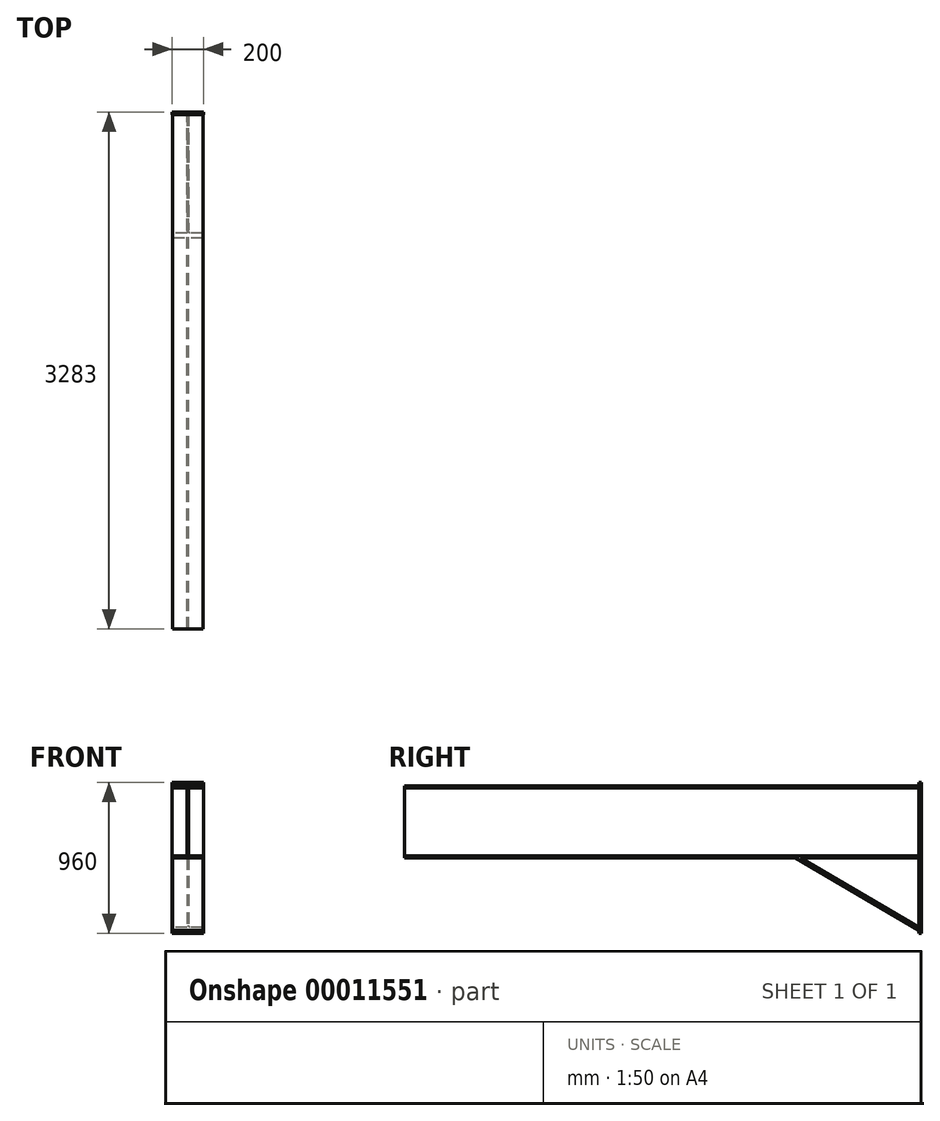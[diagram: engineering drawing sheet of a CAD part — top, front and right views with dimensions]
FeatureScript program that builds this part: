
annotation { "Feature Type Name" : "Feature", "Feature Type Description" : "" }
export const myFeature = defineFeature(function(context is Context, id is Id, definition is map)
    precondition{}
    {
        {
            var Q0;
            Q0=qCreatedBy(makeId("Front.planeOp"),FACE);
            var sketch = newSketch(context, id + "F0", { "sketchPlane" : qUnion([Q0])});
            skLineSegment(sketch, "E0.rect.bottom", {"start": v(95.5, -228.5) * mm, "end": v(-95.5, -228.5) * mm});
            skLineSegment(sketch, "E0.rect.top", {"start": v(95.5, 228.5) * mm, "end": v(-95.5, 228.5) * mm});
            skLineSegment(sketch, "E0.rect.left", {"start": v(95.5, -228.5) * mm, "end": v(95.5, -216.88) * mm});
            skLineSegment(sketch, "E0.rect.right", {"start": v(-95.5, -228.5) * mm, "end": v(-95.5, -216.88) * mm});
            skPoint(sketch, "E0.rect.middle", {"position": v(0, 0) * mm});
            skLineSegment(sketch, "E1", {"start": v(0, 228.5) * mm, "end": v(0, -228.5) * mm});
            skLineSegment(sketch, "E2.0", {"start": v(-4.25, 206.88) * mm, "end": v(-4.25, -206.88) * mm});
            skLineSegment(sketch, "E3.0", {"start": v(4.25, 206.88) * mm, "end": v(4.25, -206.88) * mm});
            skLineSegment(sketch, "E4.0", {"start": v(95.5, 216.88) * mm, "end": v(14.25, 216.88) * mm});
            skLineSegment(sketch, "E5.0", {"start": v(95.5, -216.88) * mm, "end": v(14.25, -216.88) * mm});
            skLineSegment(sketch, "E6.trimOffspring", {"start": v(-14.25, -216.88) * mm, "end": v(-95.5, -216.88) * mm});
            skLineSegment(sketch, "E7.trimOffspring", {"start": v(-14.25, 216.88) * mm, "end": v(-95.5, 216.88) * mm});
            skArc(sketch, "E8.filletArc", {"start": v(-4.25, 206.88) * mm, "mid": v(-7.18, 213.95) * mm, "end": v(-14.25, 216.88) * mm});
            skArc(sketch, "E9.filletArc", {"start": v(14.25, 216.88) * mm, "mid": v(7.18, 213.95) * mm, "end": v(4.25, 206.88) * mm});
            skArc(sketch, "E10.filletArc", {"start": v(4.25, -206.88) * mm, "mid": v(7.18, -213.95) * mm, "end": v(14.25, -216.88) * mm});
            skArc(sketch, "E11.filletArc", {"start": v(-14.25, -216.88) * mm, "mid": v(-7.18, -213.95) * mm, "end": v(-4.25, -206.88) * mm});
            skLineSegment(sketch, "E12.trimOffspring", {"start": v(-95.5, 216.88) * mm, "end": v(-95.5, 228.5) * mm});
            skLineSegment(sketch, "E13.trimOffspring", {"start": v(95.5, 216.88) * mm, "end": v(95.5, 228.5) * mm});
            skSolve(sketch);
        }
        {
            var Q0;
            Q0 = qSketchRegion(id + "F0", true);
            extrude(context, id + "F1", {"entities" : qUnion([Q0]), "depth" : 3267 * mm});
        }
        {
            var Q0;
            Q0=makeQuery(id+"F1.opExtrude","CAP_FACE",FACE,{"disambiguationData":[OSD([sQuery(id+"F0.wireOp",EDGE,"E0.rect.bottom"),sQuery(id+"F0.wireOp",EDGE,"E0.rect.top"),sQuery(id+"F0.wireOp",EDGE,"E0.rect.left"),sQuery(id+"F0.wireOp",EDGE,"E0.rect.right"),sQuery(id+"F0.wireOp",EDGE,"E2.0"),sQuery(id+"F0.wireOp",EDGE,"E3.0"),sQuery(id+"F0.wireOp",EDGE,"E4.0"),sQuery(id+"F0.wireOp",EDGE,"E5.0"),sQuery(id+"F0.wireOp",EDGE,"E6.trimOffspring"),sQuery(id+"F0.wireOp",EDGE,"E7.trimOffspring"),sQuery(id+"F0.wireOp",EDGE,"E8.filletArc"),sQuery(id+"F0.wireOp",EDGE,"E9.filletArc"),sQuery(id+"F0.wireOp",EDGE,"E10.filletArc"),sQuery(id+"F0.wireOp",EDGE,"E11.filletArc"),sQuery(id+"F0.wireOp",EDGE,"E12.trimOffspring"),sQuery(id+"F0.wireOp",EDGE,"E13.trimOffspring")])],"isStart":true});
            var sketch = newSketch(context, id + "F2", { "sketchPlane" : qUnion([Q0])});
            skLineSegment(sketch, "E14.rect.bottom", {"start": v(-100, 251.5) * mm, "end": v(100, 251.5) * mm});
            skLineSegment(sketch, "E14.rect.top", {"start": v(-100, -708.5) * mm, "end": v(100, -708.5) * mm});
            skLineSegment(sketch, "E14.rect.left", {"start": v(-100, 251.5) * mm, "end": v(-100, -708.5) * mm});
            skLineSegment(sketch, "E14.rect.right", {"start": v(100, 251.5) * mm, "end": v(100, -708.5) * mm});
            skPoint(sketch, "E14.rect.middle", {"position": v(0, -228.5) * mm});
            skSolve(sketch);
        }
        {
            var Q0;
            Q0 = qSketchRegion(id + "F2", true);
            extrude(context, id + "F3", {"entities" : qUnion([Q0]), "operationType" : NewBodyOperationType.ADD, "depth" : 16 * mm});
        }
        {
            var Q0;
            Q0=qCreatedBy(makeId("Right.planeOp"),FACE);
            var sketch = newSketch(context, id + "F4", { "sketchPlane" : qUnion([Q0])});
            skLineSegment(sketch, "E15", {"start": v(0, -228.5) * mm, "end": v(-752.27, -228.5) * mm});
            skLineSegment(sketch, "E16", {"start": v(0, -228.5) * mm, "end": v(0, -668.5) * mm});
            skLineSegment(sketch, "E17", {"start": v(0, -668.5) * mm, "end": v(-752.27, -228.5) * mm});
            skSolve(sketch);
        }
        {
            var Q0;
            Q0=makeQuery(id+"F4.imprint","IMPRINT",FACE,{"disambiguationData":[TD([[makeQuery(id+"F4.imprint","IMPRINT",EDGE,{"derivedFrom":sQuery(id+"F4.wireOp",EDGE,"E15")}),1.0]])]});
            extrude(context, id + "F5", {"entities" : qUnion([Q0]), "operationType" : NewBodyOperationType.ADD, "endBound" : BoundingType.SYMMETRIC, "depth" : 8.5 * mm});
        }
        {
            var Q0;
            Q0=qCreatedBy(makeId("Right.planeOp"),FACE);
            var sketch = newSketch(context, id + "F6", { "sketchPlane" : qUnion([Q0])});
            skLineSegment(sketch, "E18", {"start": v(0, -668.5) * mm, "end": v(0, -687.04) * mm});
            skLineSegment(sketch, "E19.0", {"start": v(0, -687.04) * mm, "end": v(-783.96, -228.5) * mm});
            skLineSegment(sketch, "E20.0", {"start": v(0, -668.5) * mm, "end": v(-752.27, -228.5) * mm});
            skLineSegment(sketch, "E21", {"start": v(-752.27, -228.5) * mm, "end": v(-783.96, -228.5) * mm});
            skSolve(sketch);
        }
        {
            var Q0;
            Q0=makeQuery(id+"F6.imprint","IMPRINT",FACE,{"disambiguationData":[TD([[makeQuery(id+"F6.imprint","IMPRINT",EDGE,{"derivedFrom":sQuery(id+"F6.wireOp",EDGE,"E18")}),-1.0]])]});
            extrude(context, id + "F7", {"entities" : qUnion([Q0]), "operationType" : NewBodyOperationType.ADD, "endBound" : BoundingType.SYMMETRIC, "depth" : 191 * mm});
        }
        {
            var Q0;
            Q0=makeQuery(id+"F5.opExtrude","CAP_EDGE",EDGE,{"disambiguationData":[OSD([sQuery(id+"F4.wireOp",EDGE,"E17")])],"isStart":true});
            var Q1;
            Q1=makeQuery(id+"F5.opExtrude","CAP_EDGE",EDGE,{"disambiguationData":[OSD([sQuery(id+"F4.wireOp",EDGE,"E17")])],"isStart":false});
            fillet(context, id + "F8", {"entities" : qUnion([Q0, Q1]), "radius" : 10 * mm, "tangentPropagation" : true, "allowEdgeOverflow" : false});
        }
    });
